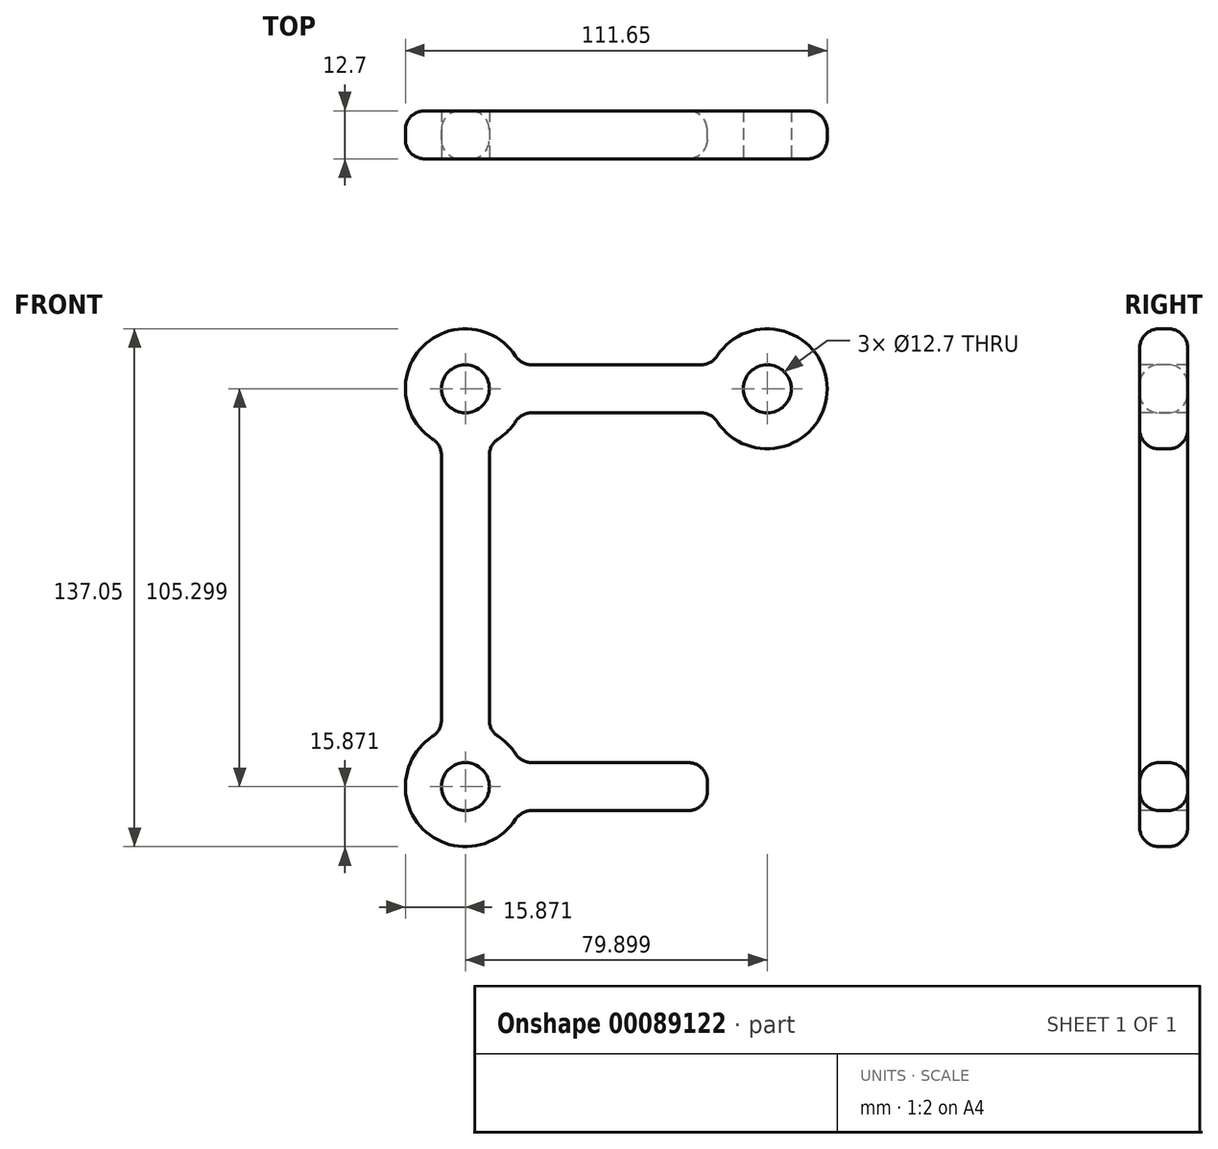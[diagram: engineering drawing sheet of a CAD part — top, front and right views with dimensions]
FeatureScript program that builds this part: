
annotation { "Feature Type Name" : "Feature", "Feature Type Description" : "" }
export const myFeature = defineFeature(function(context is Context, id is Id, definition is map)
    precondition{}
    {
        {
            var Q0;
            Q0=qCreatedBy(makeId("Front.planeOp"),FACE);
            var sketch = newSketch(context, id + "F0", { "sketchPlane" : qUnion([Q0])});
            skCircle(sketch, "E0", {"center": v(-36.35, 71) * mm, "radius": 15.88 * mm});
            skCircle(sketch, "E1", {"center": v(43.55, 71) * mm, "radius": 15.88 * mm});
            skCircle(sketch, "E2", {"center": v(-36.35, -34.3) * mm, "radius": 15.88 * mm});
            skCircle(sketch, "E3", {"center": v(43.55, -34.3) * mm, "radius": 15.88 * mm});
            skLineSegment(sketch, "E4", {"start": v(-36.35, 71) * mm, "end": v(-36.35, -34.3) * mm, "construction": true});
            skLineSegment(sketch, "E5", {"start": v(-36.35, -34.3) * mm, "end": v(43.55, -34.3) * mm, "construction": true});
            skLineSegment(sketch, "E6", {"start": v(-36.35, 71) * mm, "end": v(43.55, 71) * mm, "construction": true});
            skLineSegment(sketch, "E7", {"start": v(43.55, 71) * mm, "end": v(43.55, -34.3) * mm, "construction": true});
            skLineSegment(sketch, "E8", {"start": v(-42.7, -19.76) * mm, "end": v(-42.7, 56.44) * mm});
            skLineSegment(sketch, "E9", {"start": v(-21.8, -40.66) * mm, "end": v(29, -40.66) * mm});
            skLineSegment(sketch, "E10", {"start": v(29, 77.34) * mm, "end": v(-21.8, 77.34) * mm});
            skLineSegment(sketch, "E11.MirrorCS", {"start": v(-30, -19.76) * mm, "end": v(-30, 56.44) * mm});
            skLineSegment(sketch, "E12.MirrorCS", {"start": v(29, 64.64) * mm, "end": v(-21.8, 64.64) * mm});
            skLineSegment(sketch, "E13.MirrorCS", {"start": v(-21.8, -27.96) * mm, "end": v(29, -27.96) * mm});
            skSolve(sketch);
        }
        {
            var Q0;
            {var subQ0=sQuery(id+"F0.wireOp",EDGE,"E0");var subQ1=makeQuery(id+"F0.imprint","INTERSECT",VERTEX,{"derivedFrom":[subQ0,sQuery(id+"F0.wireOp",EDGE,"E8")]});Q0=makeQuery(id+"F0.imprint","IMPRINT",FACE,{"disambiguationData":[TD([[makeQuery(id+"F0.imprint","IMPRINT",EDGE,{"disambiguationData":[TD([[subQ1,1.0]])],"derivedFrom":subQ0}),1.0]])]});}
            var Q1;
            {var subQ0=sQuery(id+"F0.wireOp",EDGE,"E10");Q1=makeQuery(id+"F0.imprint","IMPRINT",FACE,{"disambiguationData":[TD([[makeQuery(id+"F0.imprint","IMPRINT",EDGE,{"derivedFrom":subQ0}),1.0]])]});}
            var Q2;
            {var subQ0=sQuery(id+"F0.wireOp",EDGE,"E1");var subQ3=makeQuery(id+"F0.imprint","IMPRINT",VERTEX,{"disambiguationData":[OD(0.0)],"derivedFrom":subQ0});Q2=makeQuery(id+"F0.imprint","IMPRINT",FACE,{"disambiguationData":[TD([[makeQuery(id+"F0.imprint","IMPRINT",EDGE,{"disambiguationData":[TD([[subQ3,-1.0]])],"derivedFrom":subQ0}),1.0]])]});}
            var Q3;
            {var subQ0=sQuery(id+"F0.wireOp",EDGE,"E3");var subQ1=makeQuery(id+"F0.imprint","INTERSECT",VERTEX,{"derivedFrom":[sQuery(id+"F0.wireOp",EDGE,"E9"),subQ0]});Q3=makeQuery(id+"F0.imprint","IMPRINT",FACE,{"disambiguationData":[TD([[makeQuery(id+"F0.imprint","IMPRINT",EDGE,{"disambiguationData":[TD([[subQ1,1.0]])],"derivedFrom":subQ0}),-1.0]])]});}
            var Q4;
            {var subQ0=sQuery(id+"F0.wireOp",EDGE,"E9");Q4=makeQuery(id+"F0.imprint","IMPRINT",FACE,{"disambiguationData":[TD([[makeQuery(id+"F0.imprint","IMPRINT",EDGE,{"derivedFrom":subQ0}),1.0]])]});}
            var Q5;
            {var subQ0=sQuery(id+"F0.wireOp",EDGE,"E2");var subQ1=makeQuery(id+"F0.imprint","INTERSECT",VERTEX,{"derivedFrom":[subQ0,sQuery(id+"F0.wireOp",EDGE,"E11.MirrorCS")]});Q5=makeQuery(id+"F0.imprint","IMPRINT",FACE,{"disambiguationData":[TD([[makeQuery(id+"F0.imprint","IMPRINT",EDGE,{"disambiguationData":[TD([[subQ1,1.0]])],"derivedFrom":subQ0}),1.0]])]});}
            var Q6;
            {var subQ0=sQuery(id+"F0.wireOp",EDGE,"E8");Q6=makeQuery(id+"F0.imprint","IMPRINT",FACE,{"disambiguationData":[TD([[makeQuery(id+"F0.imprint","IMPRINT",EDGE,{"derivedFrom":subQ0}),-1.0]])]});}
            extrude(context, id + "F1", {"entities" : qUnion([Q0, Q1, Q2, Q3, Q4, Q5, Q6]), "endBound" : BoundingType.SYMMETRIC, "depth" : 12.7 * mm});
        }
        {
            var Q0;
            {var subQ0=sQuery(id+"F0.wireOp",EDGE,"E1");var subQ1=makeQuery(id+"F0.imprint","INTERSECT",VERTEX,{"derivedFrom":[subQ0,sQuery(id+"F0.wireOp",EDGE,"E10")]});Q0=makeQuery(id+"F0.imprint","IMPRINT",FACE,{"disambiguationData":[TD([[makeQuery(id+"F0.imprint","IMPRINT",EDGE,{"disambiguationData":[TD([[subQ1,-1.0]])],"derivedFrom":subQ0}),1.0]])]});}
            extrude(context, id + "F2", {"entities" : qUnion([Q0]), "operationType" : NewBodyOperationType.ADD, "endBound" : BoundingType.SYMMETRIC, "depth" : 12.7 * mm});
        }
        {
            var Q0;
            Q0=makeQuery(id+"F1.opExtrude","SWEPT_FACE",FACE,{"disambiguationData":[OSD([sQuery(id+"F0.wireOp",EDGE,"E10")])]});
            var Q1;
            {var subQ0=sQuery(id+"F0.wireOp",EDGE,"E0");Q1=makeQuery(id+"F1.opExtrude","SWEPT_FACE",FACE,{"disambiguationData":[OSD([subQ0]),TDD([makeQuery(id+"F0.imprint","IMPRINT",EDGE,{"disambiguationData":[TD([[makeQuery(id+"F0.imprint","INTERSECT",VERTEX,{"derivedFrom":[subQ0,sQuery(id+"F0.wireOp",EDGE,"E8")]}),1.0]])],"derivedFrom":subQ0})])]});}
            var Q2;
            Q2=makeQuery(id+"F2.opExtrude","SWEPT_FACE",FACE,{"disambiguationData":[OSD([sQuery(id+"F0.wireOp",EDGE,"E1")])]});
            var Q3;
            {var subQ0=sQuery(id+"F0.wireOp",EDGE,"E0");Q3=makeQuery(id+"F1.opExtrude","CAP_EDGE",EDGE,{"disambiguationData":[OSD([subQ0]),TDD([makeQuery(id+"F0.imprint","IMPRINT",EDGE,{"disambiguationData":[TD([[makeQuery(id+"F0.imprint","INTERSECT",VERTEX,{"derivedFrom":[subQ0,sQuery(id+"F0.wireOp",EDGE,"E11.MirrorCS")]}),-1.0]])],"derivedFrom":subQ0})])],"isStart":false});}
            var Q4;
            {var subQ0=sQuery(id+"F0.wireOp",EDGE,"E0");Q4=makeQuery(id+"F1.opExtrude","SWEPT_FACE",FACE,{"disambiguationData":[OSD([subQ0]),TDD([makeQuery(id+"F0.imprint","IMPRINT",EDGE,{"disambiguationData":[TD([[makeQuery(id+"F0.imprint","INTERSECT",VERTEX,{"derivedFrom":[subQ0,sQuery(id+"F0.wireOp",EDGE,"E11.MirrorCS")]}),-1.0]])],"derivedFrom":subQ0})])]});}
            var Q5;
            {var subQ0=sQuery(id+"F0.wireOp",EDGE,"E1");Q5=makeQuery(id+"F2.boolean.opBoolean","MERGE",FACE,{"derivedFrom":[makeQuery(id+"F1.opExtrude","CAP_FACE",FACE,{"disambiguationData":[OSD([sQuery(id+"F0.wireOp",EDGE,"E0"),subQ0,sQuery(id+"F0.wireOp",EDGE,"E2"),sQuery(id+"F0.wireOp",EDGE,"E8"),sQuery(id+"F0.wireOp",EDGE,"E9"),sQuery(id+"F0.wireOp",EDGE,"E10"),sQuery(id+"F0.wireOp",EDGE,"E11.MirrorCS"),sQuery(id+"F0.wireOp",EDGE,"E12.MirrorCS"),sQuery(id+"F0.wireOp",EDGE,"E13.MirrorCS"),sQuery(id+"F0.wireOp",EDGE,"E3")])],"isStart":false}),makeQuery(id+"F2.opExtrude","CAP_FACE",FACE,{"disambiguationData":[OSD([subQ0])],"isStart":false})]});}
            var Q6;
            Q6=makeQuery(id+"F1.opExtrude","SWEPT_FACE",FACE,{"disambiguationData":[OSD([sQuery(id+"F0.wireOp",EDGE,"E12.MirrorCS")])]});
            var Q7;
            {var subQ0=sQuery(id+"F0.wireOp",EDGE,"E1");Q7=makeQuery(id+"F2.boolean.opBoolean","MERGE",FACE,{"derivedFrom":[makeQuery(id+"F1.opExtrude","CAP_FACE",FACE,{"disambiguationData":[OSD([sQuery(id+"F0.wireOp",EDGE,"E0"),subQ0,sQuery(id+"F0.wireOp",EDGE,"E2"),sQuery(id+"F0.wireOp",EDGE,"E8"),sQuery(id+"F0.wireOp",EDGE,"E9"),sQuery(id+"F0.wireOp",EDGE,"E10"),sQuery(id+"F0.wireOp",EDGE,"E11.MirrorCS"),sQuery(id+"F0.wireOp",EDGE,"E12.MirrorCS"),sQuery(id+"F0.wireOp",EDGE,"E13.MirrorCS"),sQuery(id+"F0.wireOp",EDGE,"E3")])],"isStart":true}),makeQuery(id+"F2.opExtrude","CAP_FACE",FACE,{"disambiguationData":[OSD([subQ0])],"isStart":true})]});}
            var Q8;
            {var subQ0=sQuery(id+"F0.wireOp",EDGE,"E0");Q8=makeQuery(id+"F1.opExtrude","CAP_EDGE",EDGE,{"disambiguationData":[OSD([subQ0]),TDD([makeQuery(id+"F0.imprint","IMPRINT",EDGE,{"disambiguationData":[TD([[makeQuery(id+"F0.imprint","INTERSECT",VERTEX,{"derivedFrom":[subQ0,sQuery(id+"F0.wireOp",EDGE,"E8")]}),1.0]])],"derivedFrom":subQ0})])],"isStart":false});}
            var Q9;
            Q9=makeQuery(id+"F1.opExtrude","SWEPT_FACE",FACE,{"disambiguationData":[OSD([sQuery(id+"F0.wireOp",EDGE,"E3")])]});
            var Q10;
            Q10=makeQuery(id+"F1.opExtrude","CAP_EDGE",EDGE,{"disambiguationData":[OSD([sQuery(id+"F0.wireOp",EDGE,"E10")])],"isStart":false});
            var Q11;
            Q11=makeQuery(id+"F1.opExtrude","SWEPT_EDGE",EDGE,{"disambiguationData":[OSD([sQuery(id+"F0.wireOp",EDGE,"E0"),sQuery(id+"F0.wireOp",EDGE,"E8")])]});
            var Q12;
            Q12=makeQuery(id+"F2.opExtrude","CAP_EDGE",EDGE,{"disambiguationData":[OSD([sQuery(id+"F0.wireOp",EDGE,"E1")])],"isStart":false});
            var Q13;
            Q13=makeQuery(id+"F1.opExtrude","SWEPT_EDGE",EDGE,{"disambiguationData":[OSD([sQuery(id+"F0.wireOp",EDGE,"E0"),sQuery(id+"F0.wireOp",EDGE,"E10")])]});
            var Q14;
            {var subQ0=sQuery(id+"F0.wireOp",EDGE,"E2");Q14=makeQuery(id+"F1.opExtrude","SWEPT_FACE",FACE,{"disambiguationData":[OSD([subQ0]),TDD([makeQuery(id+"F0.imprint","IMPRINT",EDGE,{"disambiguationData":[TD([[makeQuery(id+"F0.imprint","INTERSECT",VERTEX,{"derivedFrom":[subQ0,sQuery(id+"F0.wireOp",EDGE,"E11.MirrorCS")]}),1.0]])],"derivedFrom":subQ0})])]});}
            var Q15;
            {var subQ0=sQuery(id+"F0.wireOp",EDGE,"E2");Q15=makeQuery(id+"F1.opExtrude","SWEPT_FACE",FACE,{"disambiguationData":[OSD([subQ0]),TDD([makeQuery(id+"F0.imprint","IMPRINT",EDGE,{"disambiguationData":[TD([[makeQuery(id+"F0.imprint","INTERSECT",VERTEX,{"derivedFrom":[subQ0,sQuery(id+"F0.wireOp",EDGE,"E8")]}),-1.0]])],"derivedFrom":subQ0})])]});}
            var Q16;
            Q16=makeQuery(id+"F1.opExtrude","CAP_EDGE",EDGE,{"disambiguationData":[OSD([sQuery(id+"F0.wireOp",EDGE,"E12.MirrorCS")])],"isStart":false});
            var Q17;
            Q17=makeQuery(id+"F1.opExtrude","SWEPT_FACE",FACE,{"disambiguationData":[OSD([sQuery(id+"F0.wireOp",EDGE,"E8")])]});
            var Q18;
            Q18=makeQuery(id+"F1.opExtrude","SWEPT_EDGE",EDGE,{"disambiguationData":[OSD([sQuery(id+"F0.wireOp",EDGE,"E0"),sQuery(id+"F0.wireOp",EDGE,"E11.MirrorCS")])]});
            var Q19;
            Q19=makeQuery(id+"F1.opExtrude","SWEPT_EDGE",EDGE,{"disambiguationData":[OSD([sQuery(id+"F0.wireOp",EDGE,"E1"),sQuery(id+"F0.wireOp",EDGE,"E12.MirrorCS")])]});
            var Q20;
            Q20=makeQuery(id+"F1.opExtrude","SWEPT_FACE",FACE,{"disambiguationData":[OSD([sQuery(id+"F0.wireOp",EDGE,"E9")])]});
            var Q21;
            {var subQ0=sQuery(id+"F0.wireOp",EDGE,"E2");Q21=makeQuery(id+"F1.opExtrude","CAP_EDGE",EDGE,{"disambiguationData":[OSD([subQ0]),TDD([makeQuery(id+"F0.imprint","IMPRINT",EDGE,{"disambiguationData":[TD([[makeQuery(id+"F0.imprint","INTERSECT",VERTEX,{"derivedFrom":[subQ0,sQuery(id+"F0.wireOp",EDGE,"E8")]}),-1.0]])],"derivedFrom":subQ0})])],"isStart":false});}
            var Q22;
            Q22=makeQuery(id+"F1.opExtrude","SWEPT_EDGE",EDGE,{"disambiguationData":[OSD([sQuery(id+"F0.wireOp",EDGE,"E0"),sQuery(id+"F0.wireOp",EDGE,"E12.MirrorCS")])]});
            var Q23;
            Q23=makeQuery(id+"F1.opExtrude","CAP_EDGE",EDGE,{"disambiguationData":[OSD([sQuery(id+"F0.wireOp",EDGE,"E3")])],"isStart":false});
            var Q24;
            Q24=makeQuery(id+"F1.opExtrude","SWEPT_FACE",FACE,{"disambiguationData":[OSD([sQuery(id+"F0.wireOp",EDGE,"E11.MirrorCS")])]});
            var Q25;
            Q25=makeQuery(id+"F1.opExtrude","SWEPT_EDGE",EDGE,{"disambiguationData":[OSD([sQuery(id+"F0.wireOp",EDGE,"E1"),sQuery(id+"F0.wireOp",EDGE,"E10")])]});
            var Q26;
            Q26=makeQuery(id+"F1.opExtrude","SWEPT_FACE",FACE,{"disambiguationData":[OSD([sQuery(id+"F0.wireOp",EDGE,"E13.MirrorCS")])]});
            var Q27;
            {var subQ0=sQuery(id+"F0.wireOp",EDGE,"E0");Q27=makeQuery(id+"F1.opExtrude","CAP_EDGE",EDGE,{"disambiguationData":[OSD([subQ0]),TDD([makeQuery(id+"F0.imprint","IMPRINT",EDGE,{"disambiguationData":[TD([[makeQuery(id+"F0.imprint","INTERSECT",VERTEX,{"derivedFrom":[subQ0,sQuery(id+"F0.wireOp",EDGE,"E8")]}),1.0]])],"derivedFrom":subQ0})])],"isStart":true});}
            var Q28;
            {var subQ0=sQuery(id+"F0.wireOp",EDGE,"E0");Q28=makeQuery(id+"F1.opExtrude","CAP_EDGE",EDGE,{"disambiguationData":[OSD([subQ0]),TDD([makeQuery(id+"F0.imprint","IMPRINT",EDGE,{"disambiguationData":[TD([[makeQuery(id+"F0.imprint","INTERSECT",VERTEX,{"derivedFrom":[subQ0,sQuery(id+"F0.wireOp",EDGE,"E11.MirrorCS")]}),-1.0]])],"derivedFrom":subQ0})])],"isStart":true});}
            var Q29;
            Q29=makeQuery(id+"F1.opExtrude","CAP_EDGE",EDGE,{"disambiguationData":[OSD([sQuery(id+"F0.wireOp",EDGE,"E11.MirrorCS")])],"isStart":true});
            var Q30;
            Q30=makeQuery(id+"F1.opExtrude","SWEPT_EDGE",EDGE,{"disambiguationData":[OSD([sQuery(id+"F0.wireOp",EDGE,"E2"),sQuery(id+"F0.wireOp",EDGE,"E8")])]});
            var Q31;
            Q31=makeQuery(id+"F1.opExtrude","SWEPT_EDGE",EDGE,{"disambiguationData":[OSD([sQuery(id+"F0.wireOp",EDGE,"E2"),sQuery(id+"F0.wireOp",EDGE,"E9")])]});
            var Q32;
            Q32=makeQuery(id+"F1.opExtrude","CAP_EDGE",EDGE,{"disambiguationData":[OSD([sQuery(id+"F0.wireOp",EDGE,"E9")])],"isStart":false});
            var Q33;
            Q33=makeQuery(id+"F1.opExtrude","SWEPT_EDGE",EDGE,{"disambiguationData":[OSD([sQuery(id+"F0.wireOp",EDGE,"E9"),sQuery(id+"F0.wireOp",EDGE,"E3")])]});
            var Q34;
            Q34=makeQuery(id+"F1.opExtrude","CAP_EDGE",EDGE,{"disambiguationData":[OSD([sQuery(id+"F0.wireOp",EDGE,"E9")])],"isStart":true});
            var Q35;
            Q35=makeQuery(id+"F2.opExtrude","CAP_EDGE",EDGE,{"disambiguationData":[OSD([sQuery(id+"F0.wireOp",EDGE,"E1")])],"isStart":true});
            var Q36;
            Q36=makeQuery(id+"F1.opExtrude","CAP_EDGE",EDGE,{"disambiguationData":[OSD([sQuery(id+"F0.wireOp",EDGE,"E8")])],"isStart":false});
            var Q37;
            Q37=makeQuery(id+"F1.opExtrude","SWEPT_EDGE",EDGE,{"disambiguationData":[OSD([sQuery(id+"F0.wireOp",EDGE,"E2"),sQuery(id+"F0.wireOp",EDGE,"E11.MirrorCS")])]});
            var Q38;
            Q38=makeQuery(id+"F1.opExtrude","CAP_EDGE",EDGE,{"disambiguationData":[OSD([sQuery(id+"F0.wireOp",EDGE,"E8")])],"isStart":true});
            var Q39;
            Q39=makeQuery(id+"F1.opExtrude","CAP_EDGE",EDGE,{"disambiguationData":[OSD([sQuery(id+"F0.wireOp",EDGE,"E12.MirrorCS")])],"isStart":true});
            var Q40;
            Q40=makeQuery(id+"F1.opExtrude","CAP_EDGE",EDGE,{"disambiguationData":[OSD([sQuery(id+"F0.wireOp",EDGE,"E11.MirrorCS")])],"isStart":false});
            var Q41;
            {var subQ0=sQuery(id+"F0.wireOp",EDGE,"E2");Q41=makeQuery(id+"F1.opExtrude","CAP_EDGE",EDGE,{"disambiguationData":[OSD([subQ0]),TDD([makeQuery(id+"F0.imprint","IMPRINT",EDGE,{"disambiguationData":[TD([[makeQuery(id+"F0.imprint","INTERSECT",VERTEX,{"derivedFrom":[subQ0,sQuery(id+"F0.wireOp",EDGE,"E8")]}),-1.0]])],"derivedFrom":subQ0})])],"isStart":true});}
            var Q42;
            {var subQ0=sQuery(id+"F0.wireOp",EDGE,"E2");Q42=makeQuery(id+"F1.opExtrude","CAP_EDGE",EDGE,{"disambiguationData":[OSD([subQ0]),TDD([makeQuery(id+"F0.imprint","IMPRINT",EDGE,{"disambiguationData":[TD([[makeQuery(id+"F0.imprint","INTERSECT",VERTEX,{"derivedFrom":[subQ0,sQuery(id+"F0.wireOp",EDGE,"E11.MirrorCS")]}),1.0]])],"derivedFrom":subQ0})])],"isStart":false});}
            var Q43;
            Q43=makeQuery(id+"F1.opExtrude","SWEPT_EDGE",EDGE,{"disambiguationData":[OSD([sQuery(id+"F0.wireOp",EDGE,"E2"),sQuery(id+"F0.wireOp",EDGE,"E13.MirrorCS")])]});
            var Q44;
            Q44=makeQuery(id+"F1.opExtrude","CAP_EDGE",EDGE,{"disambiguationData":[OSD([sQuery(id+"F0.wireOp",EDGE,"E3")])],"isStart":true});
            var Q45;
            {var subQ0=sQuery(id+"F0.wireOp",EDGE,"E2");Q45=makeQuery(id+"F1.opExtrude","CAP_EDGE",EDGE,{"disambiguationData":[OSD([subQ0]),TDD([makeQuery(id+"F0.imprint","IMPRINT",EDGE,{"disambiguationData":[TD([[makeQuery(id+"F0.imprint","INTERSECT",VERTEX,{"derivedFrom":[subQ0,sQuery(id+"F0.wireOp",EDGE,"E11.MirrorCS")]}),1.0]])],"derivedFrom":subQ0})])],"isStart":true});}
            var Q46;
            Q46=makeQuery(id+"F1.opExtrude","SWEPT_EDGE",EDGE,{"disambiguationData":[OSD([sQuery(id+"F0.wireOp",EDGE,"E13.MirrorCS"),sQuery(id+"F0.wireOp",EDGE,"E3")])]});
            var Q47;
            Q47=makeQuery(id+"F1.opExtrude","CAP_EDGE",EDGE,{"disambiguationData":[OSD([sQuery(id+"F0.wireOp",EDGE,"E13.MirrorCS")])],"isStart":false});
            var Q48;
            Q48=makeQuery(id+"F1.opExtrude","CAP_EDGE",EDGE,{"disambiguationData":[OSD([sQuery(id+"F0.wireOp",EDGE,"E13.MirrorCS")])],"isStart":true});
            fillet(context, id + "F3", {"entities" : qUnion([Q0, Q1, Q2, Q3, Q4, Q5, Q6, Q7, Q8, Q9, Q10, Q11, Q12, Q13, Q14, Q15, Q16, Q17, Q18, Q19, Q20, Q21, Q22, Q23, Q24, Q25, Q26, Q27, Q28, Q29, Q30, Q31, Q32, Q33, Q34, Q35, Q36, Q37, Q38, Q39, Q40, Q41, Q42, Q43, Q44, Q45, Q46, Q47, Q48]), "radius" : 5.08 * mm, "tangentPropagation" : true, "allowEdgeOverflow" : false});
        }
        {
            var Q0;
            {var subQ0=sQuery(id+"F0.wireOp",EDGE,"E1");Q0=makeQuery(id+"F2.boolean.opBoolean","MERGE",FACE,{"derivedFrom":[makeQuery(id+"F1.opExtrude","CAP_FACE",FACE,{"disambiguationData":[OSD([sQuery(id+"F0.wireOp",EDGE,"E0"),subQ0,sQuery(id+"F0.wireOp",EDGE,"E2"),sQuery(id+"F0.wireOp",EDGE,"E8"),sQuery(id+"F0.wireOp",EDGE,"E9"),sQuery(id+"F0.wireOp",EDGE,"E10"),sQuery(id+"F0.wireOp",EDGE,"E11.MirrorCS"),sQuery(id+"F0.wireOp",EDGE,"E12.MirrorCS"),sQuery(id+"F0.wireOp",EDGE,"E13.MirrorCS"),sQuery(id+"F0.wireOp",EDGE,"E3")])],"isStart":false}),makeQuery(id+"F2.opExtrude","CAP_FACE",FACE,{"disambiguationData":[OSD([subQ0])],"isStart":false})]});}
            var sketch = newSketch(context, id + "F4", { "sketchPlane" : qUnion([Q0])});
            skCircle(sketch, "E14", {"center": v(-36.35, 71) * mm, "radius": 6.35 * mm});
            skCircle(sketch, "E15", {"center": v(43.55, 71) * mm, "radius": 6.35 * mm});
            skCircle(sketch, "E16", {"center": v(43.55, -34.3) * mm, "radius": 6.35 * mm});
            skCircle(sketch, "E17", {"center": v(-36.35, -34.3) * mm, "radius": 6.35 * mm});
            skSolve(sketch);
        }
        {
            var Q0;
            Q0=makeQuery(id+"F4.imprint","IMPRINT",FACE,{"disambiguationData":[TD([[makeQuery(id+"F4.imprint","IMPRINT",EDGE,{"derivedFrom":sQuery(id+"F4.wireOp",EDGE,"E14")}),1.0]])]});
            var Q1;
            Q1=makeQuery(id+"F4.imprint","IMPRINT",FACE,{"disambiguationData":[TD([[makeQuery(id+"F4.imprint","IMPRINT",EDGE,{"derivedFrom":sQuery(id+"F4.wireOp",EDGE,"E15")}),1.0]])]});
            var Q2;
            Q2=makeQuery(id+"F4.imprint","IMPRINT",FACE,{"disambiguationData":[TD([[makeQuery(id+"F4.imprint","IMPRINT",EDGE,{"derivedFrom":sQuery(id+"F4.wireOp",EDGE,"E17")}),1.0]])]});
            var Q3;
            Q3=makeQuery(id+"F4.imprint","IMPRINT",FACE,{"disambiguationData":[TD([[makeQuery(id+"F4.imprint","IMPRINT",EDGE,{"derivedFrom":sQuery(id+"F4.wireOp",EDGE,"E16")}),1.0]])]});
            var Q4;
            Q4=sQuery(id+"F4.wireOp",EDGE,"E14");
            var Q5;
            Q5=sQuery(id+"F4.wireOp",EDGE,"E15");
            var Q6;
            Q6=sQuery(id+"F4.wireOp",EDGE,"E16");
            var Q7;
            Q7=sQuery(id+"F4.wireOp",EDGE,"E17");
            extrude(context, id + "F5", {"entities" : qUnion([Q0, Q1, Q2, Q3]), "operationType" : NewBodyOperationType.REMOVE, "surfaceEntities" : qUnion([Q4, Q5, Q6, Q7]), "endBound" : BoundingType.THROUGH_ALL, "oppositeDirection" : true, "depth" : 25.4 * mm});
        }
        {
            var Q0;
            Q0=makeQuery(id+"F1.opExtrude","SWEPT_BODY",BODY,{"disambiguationData":[OSD([sQuery(id+"F0.wireOp",EDGE,"E0"),sQuery(id+"F0.wireOp",EDGE,"E1"),sQuery(id+"F0.wireOp",EDGE,"E2"),sQuery(id+"F0.wireOp",EDGE,"E8"),sQuery(id+"F0.wireOp",EDGE,"E9"),sQuery(id+"F0.wireOp",EDGE,"E10"),sQuery(id+"F0.wireOp",EDGE,"E11.MirrorCS"),sQuery(id+"F0.wireOp",EDGE,"E12.MirrorCS"),sQuery(id+"F0.wireOp",EDGE,"E13.MirrorCS"),sQuery(id+"F0.wireOp",EDGE,"E3")])]});
            var Q1;
            Q1=qCreatedBy(makeId("Front.planeOp"),FACE);
            transform(context, id + "F6", {"entities" : qUnion([Q0]), "transformType" : TransformType.TRANSLATION_DISTANCE, "transformDirection" : qUnion([Q1]), "distance" : 25.4 * mm, "makeCopy" : false});
        }
    });
